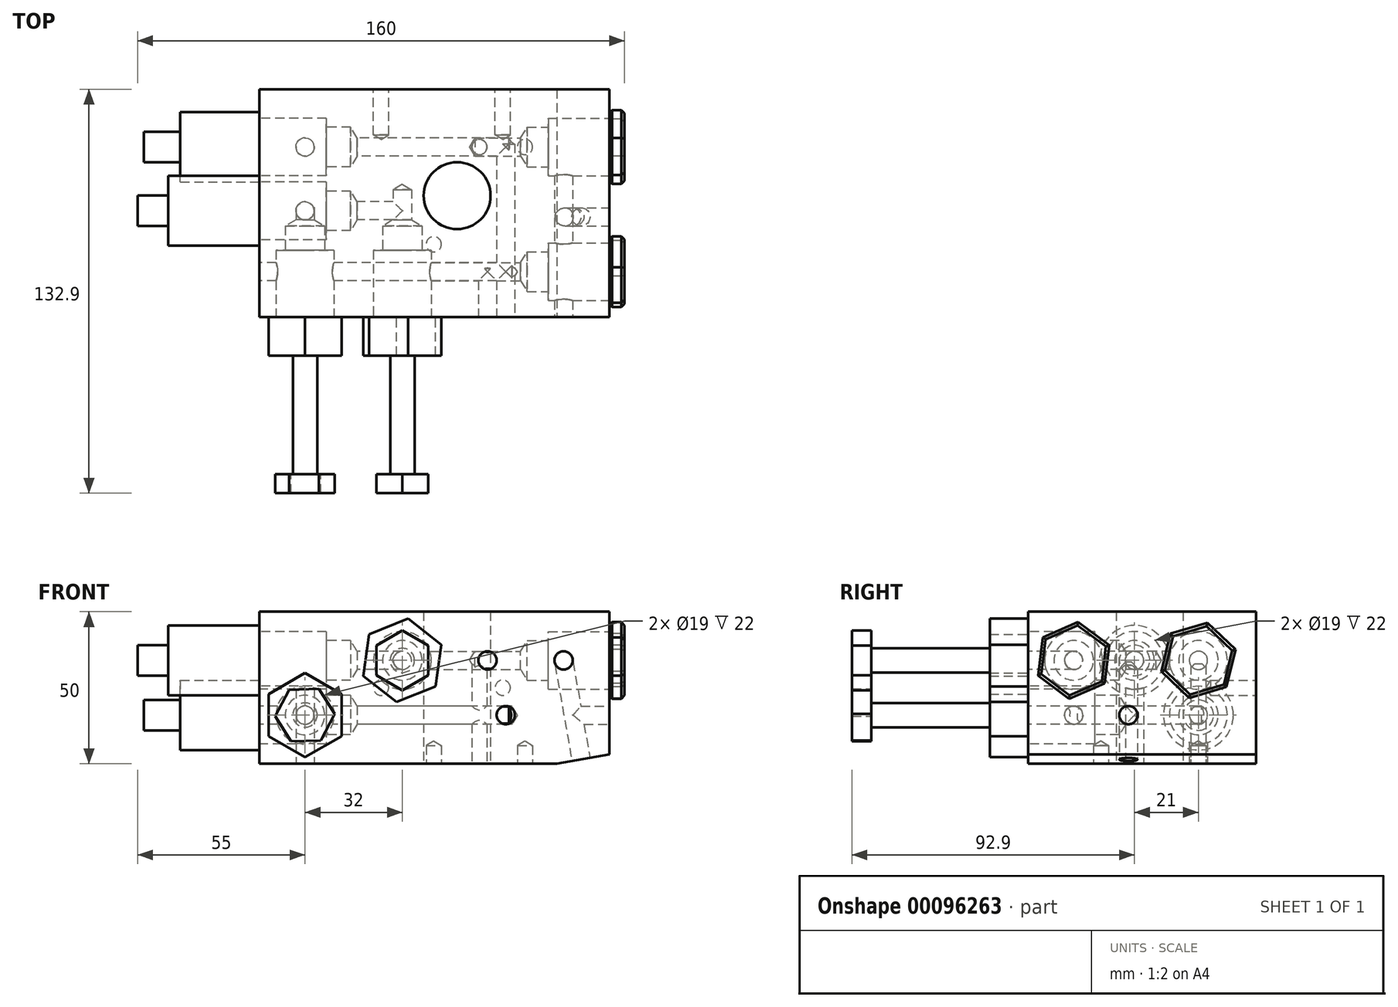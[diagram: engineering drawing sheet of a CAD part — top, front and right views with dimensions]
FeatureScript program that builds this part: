
annotation { "Feature Type Name" : "Feature", "Feature Type Description" : "" }
export const myFeature = defineFeature(function(context is Context, id is Id, definition is map)
    precondition{}
    {
        {
            var Q0;
            Q0=qCreatedBy(makeId("Top.planeOp"),FACE);
            var sketch = newSketch(context, id + "F0", { "sketchPlane" : qUnion([Q0])});
            skLineSegment(sketch, "E0.rect.bottom", {"start": v(50, 35) * mm, "end": v(-65, 35) * mm});
            skLineSegment(sketch, "E0.rect.top", {"start": v(50, -40) * mm, "end": v(-65, -40) * mm});
            skLineSegment(sketch, "E0.rect.left", {"start": v(50, 35) * mm, "end": v(50, -40) * mm});
            skLineSegment(sketch, "E0.rect.right", {"start": v(-65, 35) * mm, "end": v(-65, -40) * mm});
            skPoint(sketch, "E0.rect.middle", {"position": v(0, 0) * mm});
            skSolve(sketch);
        }
        {
            var Q0;
            Q0=makeQuery(id+"F0.imprint","IMPRINT",FACE,{"disambiguationData":[TD([[makeQuery(id+"F0.imprint","IMPRINT",EDGE,{"derivedFrom":sQuery(id+"F0.wireOp",EDGE,"E0.rect.bottom")}),1.0]])]});
            var Q1;
            Q1=makeQuery(id+"F0.imprint","IMPRINT",FACE,{"disambiguationData":[TD([[makeQuery(id+"F0.imprint","IMPRINT",EDGE,{"derivedFrom":sQuery(id+"F0.wireOp",EDGE,"7588558b-6d4b-4371-8287-17bf13519ebf.1.0.0")}),1.0]])]});
            var Q2;
            Q2=makeQuery(id+"F0.imprint","IMPRINT",FACE,{"disambiguationData":[TD([[makeQuery(id+"F0.imprint","IMPRINT",EDGE,{"derivedFrom":sQuery(id+"F0.wireOp",EDGE,"7588558b-6d4b-4371-8287-17bf13519ebf.1.1.0")}),1.0]])]});
            var Q3;
            Q3=makeQuery(id+"F0.imprint","IMPRINT",FACE,{"disambiguationData":[TD([[makeQuery(id+"F0.imprint","IMPRINT",EDGE,{"derivedFrom":sQuery(id+"F0.wireOp",EDGE,"f2f94a69-6f03-48d5-8e05-4ef8c2e551b9")}),1.0]])]});
            var Q4;
            Q4=makeQuery(id+"F0.imprint","IMPRINT",FACE,{"disambiguationData":[TD([[makeQuery(id+"F0.imprint","IMPRINT",EDGE,{"derivedFrom":sQuery(id+"F0.wireOp",EDGE,"7588558b-6d4b-4371-8287-17bf13519ebf.0.1.0")}),1.0]])]});
            extrude(context, id + "F1", {"entities" : qUnion([Q0, Q1, Q2, Q3, Q4]), "depth" : 50 * mm});
        }
        {
            var Q0;
            Q0=makeQuery(id+"F1.opExtrude","CAP_FACE",FACE,{"disambiguationData":[OSD([sQuery(id+"F0.wireOp",EDGE,"E0.rect.bottom"),sQuery(id+"F0.wireOp",EDGE,"E0.rect.top"),sQuery(id+"F0.wireOp",EDGE,"E0.rect.left"),sQuery(id+"F0.wireOp",EDGE,"E0.rect.right"),sQuery(id+"F0.wireOp",EDGE,"fc206ab4-4ad2-4e77-9b30-4fb9f0a5357b")])],"isStart":true});
            var sketch = newSketch(context, id + "F2", { "sketchPlane" : qUnion([Q0])});
            skCircle(sketch, "E1", {"center": v(22.32, -16) * mm, "radius": 2.75 * mm});
            skCircle(sketch, "E2", {"center": v(-7.68, 16) * mm, "radius": 2.75 * mm});
            skCircle(sketch, "E3", {"center": v(7.32, -16) * mm, "radius": 3 * mm});
            skPoint(sketch, "E4", {"position": v(-50, 5) * mm});
            skPoint(sketch, "E5", {"position": v(-50, -16) * mm});
            skLineSegment(sketch, "E6", {"start": v(7.32, -16) * mm, "end": v(44.16, -16) * mm, "construction": true});
            skLineSegment(sketch, "E7", {"start": v(7.32, -16) * mm, "end": v(7.32, 33.05) * mm, "construction": true});
            skPoint(sketch, "E8.0", {"position": v(0, 0) * mm});
            skLineSegment(sketch, "E9", {"start": v(-80.64, 0) * mm, "end": v(41.16, 0) * mm, "construction": true});
            skSolve(sketch);
        }
        {
            var Q0;
            Q0=sQuery(id+"F2.wireOp",VERTEX,"E3.center");
            var Q1;
            Q1=makeQuery(id+"F1.opExtrude","SWEPT_BODY",BODY,{"disambiguationData":[OSD([sQuery(id+"F0.wireOp",EDGE,"E0.rect.bottom"),sQuery(id+"F0.wireOp",EDGE,"E0.rect.top"),sQuery(id+"F0.wireOp",EDGE,"E0.rect.left"),sQuery(id+"F0.wireOp",EDGE,"E0.rect.right"),sQuery(id+"F0.wireOp",EDGE,"fc206ab4-4ad2-4e77-9b30-4fb9f0a5357b")])]});
            hole(context, id + "F3", {"style" : HoleStyle.SIMPLE, "holeDiameter" : 5 * mm, "endStyle" : HoleEndStyle.BLIND, "holeDepth" : 35 * mm, "locations" : qUnion([Q0]), "scope" : qUnion([Q1])});
        }
        {
            var Q0;
            Q0=makeQuery(id+"F1.opExtrude","SWEPT_FACE",FACE,{"disambiguationData":[OSD([sQuery(id+"F0.wireOp",EDGE,"E0.rect.left")])]});
            var sketch = newSketch(context, id + "F4", { "sketchPlane" : qUnion([Q0])});
            skLineSegment(sketch, "E10", {"start": v(-25, 34) * mm, "end": v(16, 34) * mm, "construction": true});
            skPoint(sketch, "E11", {"position": v(16, 34) * mm});
            skPoint(sketch, "E12", {"position": v(-25, 34) * mm});
            skCircle(sketch, "E13.cCircle", {"center": v(-25, 34) * mm, "radius": 11 * mm, "construction": true});
            skLineSegment(sketch, "E13.0", {"start": v(-35.19, 41.58) * mm, "end": v(-23.53, 46.62) * mm});
            skLineSegment(sketch, "E13.1", {"start": v(-23.53, 46.62) * mm, "end": v(-13.34, 39.03) * mm});
            skLineSegment(sketch, "E13.2", {"start": v(-13.34, 39.03) * mm, "end": v(-14.81, 26.42) * mm});
            skLineSegment(sketch, "E13.3", {"start": v(-14.81, 26.42) * mm, "end": v(-26.47, 21.38) * mm});
            skLineSegment(sketch, "E13.4", {"start": v(-26.47, 21.38) * mm, "end": v(-36.66, 28.97) * mm});
            skLineSegment(sketch, "E13.5", {"start": v(-36.66, 28.97) * mm, "end": v(-35.19, 41.58) * mm});
            skPoint(sketch, "E13.0.midPoint", {"position": v(-29.36, 44.1) * mm});
            skCircle(sketch, "E14.cCircle", {"center": v(16, 34) * mm, "radius": 11 * mm, "construction": true});
            skLineSegment(sketch, "E14.0", {"start": v(6.8, 42.75) * mm, "end": v(18.98, 46.35) * mm});
            skLineSegment(sketch, "E14.1", {"start": v(18.98, 46.35) * mm, "end": v(28.18, 37.6) * mm});
            skLineSegment(sketch, "E14.2", {"start": v(28.18, 37.6) * mm, "end": v(25.2, 25.25) * mm});
            skLineSegment(sketch, "E14.3", {"start": v(25.2, 25.25) * mm, "end": v(13.02, 21.65) * mm});
            skLineSegment(sketch, "E14.4", {"start": v(13.02, 21.65) * mm, "end": v(3.82, 30.4) * mm});
            skLineSegment(sketch, "E14.5", {"start": v(3.82, 30.4) * mm, "end": v(6.8, 42.75) * mm});
            skPoint(sketch, "E14.0.midPoint", {"position": v(12.89, 44.55) * mm});
            skPoint(sketch, "E15", {"position": v(-7, 16) * mm});
            skSolve(sketch);
        }
        {
            var Q0;
            Q0=sQuery(id+"F4.wireOp",VERTEX,"E11");
            var Q1;
            Q1=sQuery(id+"F4.wireOp",VERTEX,"E12");
            var Q2;
            Q2=makeQuery(id+"F1.opExtrude","SWEPT_BODY",BODY,{"disambiguationData":[OSD([sQuery(id+"F0.wireOp",EDGE,"E0.rect.bottom"),sQuery(id+"F0.wireOp",EDGE,"E0.rect.top"),sQuery(id+"F0.wireOp",EDGE,"E0.rect.left"),sQuery(id+"F0.wireOp",EDGE,"E0.rect.right"),sQuery(id+"F0.wireOp",EDGE,"fc206ab4-4ad2-4e77-9b30-4fb9f0a5357b")])]});
            hole(context, id + "F5", {"style" : HoleStyle.C_BORE, "endStyle" : HoleEndStyle.BLIND, "holeDiameter" : 13 * mm, "cBoreDiameter" : 19 * mm, "cBoreDepth" : 20 * mm, "holeDepth" : 27 * mm, "locations" : qUnion([Q0, Q1]), "scope" : qUnion([Q2])});
        }
        {
            var Q0;
            Q0=makeQuery(id+"F1.opExtrude","SWEPT_FACE",FACE,{"disambiguationData":[OSD([sQuery(id+"F0.wireOp",EDGE,"E0.rect.top")])]});
            var sketch = newSketch(context, id + "F6", { "sketchPlane" : qUnion([Q0])});
            skLineSegment(sketch, "E16", {"start": v(-65, 34) * mm, "end": v(50, 34) * mm, "construction": true});
            skLineSegment(sketch, "E17", {"start": v(-65, 16) * mm, "end": v(50, 16) * mm, "construction": true});
            skPoint(sketch, "E18", {"position": v(-50, 16) * mm});
            skPoint(sketch, "E19", {"position": v(-18, 34) * mm});
            skPoint(sketch, "E20", {"position": v(35, 34) * mm});
            skPoint(sketch, "E21", {"position": v(10, 34) * mm});
            skPoint(sketch, "E22", {"position": v(16, 16) * mm});
            skLineSegment(sketch, "E23", {"start": v(32.84, 0) * mm, "end": v(50, 3.03) * mm});
            skSolve(sketch);
        }
        {
            var Q0;
            Q0=sQuery(id+"F6.wireOp",VERTEX,"E22");
            var Q1;
            Q1=makeQuery(id+"F1.opExtrude","SWEPT_BODY",BODY,{"disambiguationData":[OSD([sQuery(id+"F0.wireOp",EDGE,"E0.rect.bottom"),sQuery(id+"F0.wireOp",EDGE,"E0.rect.top"),sQuery(id+"F0.wireOp",EDGE,"E0.rect.left"),sQuery(id+"F0.wireOp",EDGE,"E0.rect.right"),sQuery(id+"F0.wireOp",EDGE,"fc206ab4-4ad2-4e77-9b30-4fb9f0a5357b")])]});
            hole(context, id + "F7", {"style" : HoleStyle.SIMPLE, "holeDiameter" : 6 * mm, "endStyle" : HoleEndStyle.BLIND, "holeDepth" : 57 * mm, "locations" : qUnion([Q0]), "scope" : qUnion([Q1])});
        }
        {
            var Q0;
            Q0=makeQuery(id+"F1.opExtrude","SWEPT_FACE",FACE,{"disambiguationData":[OSD([sQuery(id+"F0.wireOp",EDGE,"E0.rect.right")])]});
            var sketch = newSketch(context, id + "F8", { "sketchPlane" : qUnion([Q0])});
            skPoint(sketch, "E24", {"position": v(25, 16) * mm});
            skPoint(sketch, "E25", {"position": v(5, 34) * mm});
            skPoint(sketch, "E26", {"position": v(-16, 16) * mm});
            skCircle(sketch, "E27", {"center": v(5, 34) * mm, "radius": 11.5 * mm});
            skSolve(sketch);
        }
        {
            var Q0;
            Q0=sQuery(id+"F8.wireOp",VERTEX,"E24");
            var Q1;
            Q1=makeQuery(id+"F1.opExtrude","SWEPT_BODY",BODY,{"disambiguationData":[OSD([sQuery(id+"F0.wireOp",EDGE,"E0.rect.bottom"),sQuery(id+"F0.wireOp",EDGE,"E0.rect.top"),sQuery(id+"F0.wireOp",EDGE,"E0.rect.left"),sQuery(id+"F0.wireOp",EDGE,"E0.rect.right"),sQuery(id+"F0.wireOp",EDGE,"fc206ab4-4ad2-4e77-9b30-4fb9f0a5357b")])]});
            hole(context, id + "F9", {"style" : HoleStyle.SIMPLE, "endStyle" : HoleEndStyle.BLIND, "holeDiameter" : 6 * mm, "holeDepth" : 83 * mm, "locations" : qUnion([Q0]), "scope" : qUnion([Q1])});
        }
        {
            var Q0;
            Q0=sQuery(id+"F6.wireOp",VERTEX,"E18");
            var Q1;
            Q1=sQuery(id+"F6.wireOp",VERTEX,"E19");
            var Q2;
            Q2=makeQuery(id+"F1.opExtrude","SWEPT_BODY",BODY,{"disambiguationData":[OSD([sQuery(id+"F0.wireOp",EDGE,"E0.rect.bottom"),sQuery(id+"F0.wireOp",EDGE,"E0.rect.top"),sQuery(id+"F0.wireOp",EDGE,"E0.rect.left"),sQuery(id+"F0.wireOp",EDGE,"E0.rect.right"),sQuery(id+"F0.wireOp",EDGE,"fc206ab4-4ad2-4e77-9b30-4fb9f0a5357b")])]});
            hole(context, id + "F10", {"style" : HoleStyle.C_BORE, "endStyle" : HoleEndStyle.BLIND, "holeDiameter" : 13 * mm, "cBoreDiameter" : 19 * mm, "cBoreDepth" : 22 * mm, "holeDepth" : 30 * mm, "locations" : qUnion([Q0, Q1]), "scope" : qUnion([Q2])});
        }
        {
            var Q0;
            Q0=sQuery(id+"F6.wireOp",VERTEX,"E18");
            var Q1;
            Q1=makeQuery(id+"F1.opExtrude","SWEPT_BODY",BODY,{"disambiguationData":[OSD([sQuery(id+"F0.wireOp",EDGE,"E0.rect.bottom"),sQuery(id+"F0.wireOp",EDGE,"E0.rect.top"),sQuery(id+"F0.wireOp",EDGE,"E0.rect.left"),sQuery(id+"F0.wireOp",EDGE,"E0.rect.right"),sQuery(id+"F0.wireOp",EDGE,"fc206ab4-4ad2-4e77-9b30-4fb9f0a5357b")])]});
            hole(context, id + "F11", {"style" : HoleStyle.SIMPLE, "endStyle" : HoleEndStyle.BLIND, "holeDiameter" : 6 * mm, "holeDepth" : 4 * mm, "locations" : qUnion([Q0]), "scope" : qUnion([Q1])});
        }
        {
            var Q0;
            Q0=sQuery(id+"F4.wireOp",VERTEX,"E11");
            var Q1;
            Q1=makeQuery(id+"F1.opExtrude","SWEPT_BODY",BODY,{"disambiguationData":[OSD([sQuery(id+"F0.wireOp",EDGE,"E0.rect.bottom"),sQuery(id+"F0.wireOp",EDGE,"E0.rect.top"),sQuery(id+"F0.wireOp",EDGE,"E0.rect.left"),sQuery(id+"F0.wireOp",EDGE,"E0.rect.right"),sQuery(id+"F0.wireOp",EDGE,"fc206ab4-4ad2-4e77-9b30-4fb9f0a5357b")])]});
            hole(context, id + "F12", {"style" : HoleStyle.SIMPLE, "endStyle" : HoleEndStyle.BLIND, "holeDiameter" : 6 * mm, "holeDepth" : 15 * mm, "locations" : qUnion([Q0]), "scope" : qUnion([Q1])});
        }
        {
            var Q0;
            Q0=sQuery(id+"F6.wireOp",VERTEX,"E21");
            var Q1;
            Q1=makeQuery(id+"F1.opExtrude","SWEPT_BODY",BODY,{"disambiguationData":[OSD([sQuery(id+"F0.wireOp",EDGE,"E0.rect.bottom"),sQuery(id+"F0.wireOp",EDGE,"E0.rect.top"),sQuery(id+"F0.wireOp",EDGE,"E0.rect.left"),sQuery(id+"F0.wireOp",EDGE,"E0.rect.right"),sQuery(id+"F0.wireOp",EDGE,"fc206ab4-4ad2-4e77-9b30-4fb9f0a5357b")])]});
            hole(context, id + "F13", {"style" : HoleStyle.SIMPLE, "endStyle" : HoleEndStyle.BLIND, "holeDiameter" : 6 * mm, "holeDepth" : 16 * mm, "locations" : qUnion([Q0]), "scope" : qUnion([Q1])});
        }
        {
            var Q0;
            Q0=sQuery(id+"F4.wireOp",VERTEX,"E12");
            var Q1;
            Q1=makeQuery(id+"F1.opExtrude","SWEPT_BODY",BODY,{"disambiguationData":[OSD([sQuery(id+"F0.wireOp",EDGE,"E0.rect.bottom"),sQuery(id+"F0.wireOp",EDGE,"E0.rect.top"),sQuery(id+"F0.wireOp",EDGE,"E0.rect.left"),sQuery(id+"F0.wireOp",EDGE,"E0.rect.right"),sQuery(id+"F0.wireOp",EDGE,"fc206ab4-4ad2-4e77-9b30-4fb9f0a5357b")])]});
            hole(context, id + "F14", {"style" : HoleStyle.SIMPLE, "endStyle" : HoleEndStyle.BLIND, "holeDiameter" : 6 * mm, "holeDepth" : 30 * mm, "locations" : qUnion([Q0]), "scope" : qUnion([Q1])});
        }
        {
            var Q0;
            Q0=sQuery(id+"F6.wireOp",VERTEX,"E20");
            var Q1;
            Q1=makeQuery(id+"F1.opExtrude","SWEPT_BODY",BODY,{"disambiguationData":[OSD([sQuery(id+"F0.wireOp",EDGE,"E0.rect.bottom"),sQuery(id+"F0.wireOp",EDGE,"E0.rect.top"),sQuery(id+"F0.wireOp",EDGE,"E0.rect.left"),sQuery(id+"F0.wireOp",EDGE,"E0.rect.right"),sQuery(id+"F0.wireOp",EDGE,"fc206ab4-4ad2-4e77-9b30-4fb9f0a5357b")])]});
            hole(context, id + "F15", {"style" : HoleStyle.SIMPLE, "endStyle" : HoleEndStyle.BLIND, "holeDiameter" : 6 * mm, "holeDepth" : 50 * mm, "locations" : qUnion([Q0]), "scope" : qUnion([Q1])});
        }
        {
            var Q0;
            Q0=sQuery(id+"F8.wireOp",VERTEX,"E25");
            var Q1;
            Q1=makeQuery(id+"F1.opExtrude","SWEPT_BODY",BODY,{"disambiguationData":[OSD([sQuery(id+"F0.wireOp",EDGE,"E0.rect.bottom"),sQuery(id+"F0.wireOp",EDGE,"E0.rect.top"),sQuery(id+"F0.wireOp",EDGE,"E0.rect.left"),sQuery(id+"F0.wireOp",EDGE,"E0.rect.right"),sQuery(id+"F0.wireOp",EDGE,"fc206ab4-4ad2-4e77-9b30-4fb9f0a5357b")])]});
            hole(context, id + "F16", {"style" : HoleStyle.C_BORE, "endStyle" : HoleEndStyle.BLIND, "holeDiameter" : 13 * mm, "cBoreDiameter" : 19 * mm, "cBoreDepth" : 22 * mm, "holeDepth" : 30 * mm, "locations" : qUnion([Q0]), "scope" : qUnion([Q1])});
        }
        {
            var Q0;
            Q0=sQuery(id+"F8.wireOp",VERTEX,"E26");
            var Q1;
            Q1=makeQuery(id+"F1.opExtrude","SWEPT_BODY",BODY,{"disambiguationData":[OSD([sQuery(id+"F0.wireOp",EDGE,"E0.rect.bottom"),sQuery(id+"F0.wireOp",EDGE,"E0.rect.top"),sQuery(id+"F0.wireOp",EDGE,"E0.rect.left"),sQuery(id+"F0.wireOp",EDGE,"E0.rect.right")])]});
            hole(context, id + "F17", {"style" : HoleStyle.C_BORE, "endStyle" : HoleEndStyle.BLIND, "holeDiameter" : 13 * mm, "cBoreDiameter" : 19 * mm, "cBoreDepth" : 22 * mm, "holeDepth" : 30 * mm, "startFromSketch" : true, "locations" : qUnion([Q0]), "scope" : qUnion([Q1])});
        }
        {
            var Q0;
            Q0=sQuery(id+"F8.wireOp",VERTEX,"E25");
            var Q1;
            Q1=makeQuery(id+"F1.opExtrude","SWEPT_BODY",BODY,{"disambiguationData":[OSD([sQuery(id+"F0.wireOp",EDGE,"E0.rect.bottom"),sQuery(id+"F0.wireOp",EDGE,"E0.rect.top"),sQuery(id+"F0.wireOp",EDGE,"E0.rect.left"),sQuery(id+"F0.wireOp",EDGE,"E0.rect.right"),sQuery(id+"F0.wireOp",EDGE,"fc206ab4-4ad2-4e77-9b30-4fb9f0a5357b")])]});
            hole(context, id + "F18", {"style" : HoleStyle.SIMPLE, "endStyle" : HoleEndStyle.BLIND, "holeDiameter" : 6 * mm, "holeDepth" : 15 * mm, "locations" : qUnion([Q0]), "scope" : qUnion([Q1])});
        }
        {
            var Q0;
            Q0=sQuery(id+"F2.wireOp",VERTEX,"E4");
            var Q1;
            Q1=makeQuery(id+"F1.opExtrude","SWEPT_BODY",BODY,{"disambiguationData":[OSD([sQuery(id+"F0.wireOp",EDGE,"E0.rect.bottom"),sQuery(id+"F0.wireOp",EDGE,"E0.rect.top"),sQuery(id+"F0.wireOp",EDGE,"E0.rect.left"),sQuery(id+"F0.wireOp",EDGE,"E0.rect.right"),sQuery(id+"F0.wireOp",EDGE,"fc206ab4-4ad2-4e77-9b30-4fb9f0a5357b")])]});
            hole(context, id + "F19", {"style" : HoleStyle.SIMPLE, "endStyle" : HoleEndStyle.BLIND, "holeDiameter" : 6 * mm, "holeDepth" : 35 * mm, "locations" : qUnion([Q0]), "scope" : qUnion([Q1])});
        }
        {
            var Q0;
            Q0=sQuery(id+"F6.wireOp",VERTEX,"E19");
            var Q1;
            Q1=makeQuery(id+"F1.opExtrude","SWEPT_BODY",BODY,{"disambiguationData":[OSD([sQuery(id+"F0.wireOp",EDGE,"E0.rect.bottom"),sQuery(id+"F0.wireOp",EDGE,"E0.rect.top"),sQuery(id+"F0.wireOp",EDGE,"E0.rect.left"),sQuery(id+"F0.wireOp",EDGE,"E0.rect.right"),sQuery(id+"F0.wireOp",EDGE,"fc206ab4-4ad2-4e77-9b30-4fb9f0a5357b")])]});
            hole(context, id + "F20", {"style" : HoleStyle.SIMPLE, "endStyle" : HoleEndStyle.BLIND, "holeDiameter" : 6 * mm, "holeDepth" : 4 * mm, "locations" : qUnion([Q0]), "scope" : qUnion([Q1])});
        }
        {
            var Q0;
            Q0=makeQuery(id+"F1.opExtrude","SWEPT_FACE",FACE,{"disambiguationData":[OSD([sQuery(id+"F0.wireOp",EDGE,"E0.rect.bottom")])]});
            var sketch = newSketch(context, id + "F21", { "sketchPlane" : qUnion([Q0])});
            skPoint(sketch, "E28", {"position": v(-15, 25) * mm});
            skPoint(sketch, "E29.1.0.0", {"position": v(25, 25) * mm});
            skLineSegment(sketch, "E29.direction1", {"start": v(-15, 25) * mm, "end": v(25, 25) * mm, "construction": true});
            skSolve(sketch);
        }
        {
            var Q0;
            Q0=sQuery(id+"F21.wireOp",VERTEX,"E29.1.0.0");
            var Q1;
            Q1=sQuery(id+"F21.wireOp",VERTEX,"E28");
            var Q2;
            Q2=makeQuery(id+"F1.opExtrude","SWEPT_BODY",BODY,{"disambiguationData":[OSD([sQuery(id+"F0.wireOp",EDGE,"E0.rect.bottom"),sQuery(id+"F0.wireOp",EDGE,"E0.rect.top"),sQuery(id+"F0.wireOp",EDGE,"E0.rect.left"),sQuery(id+"F0.wireOp",EDGE,"E0.rect.right"),sQuery(id+"F0.wireOp",EDGE,"fc206ab4-4ad2-4e77-9b30-4fb9f0a5357b")])]});
            hole(context, id + "F22", {"style" : HoleStyle.SIMPLE, "endStyle" : HoleEndStyle.BLIND, "holeDiameter" : 5 * mm, "holeDepth" : 15 * mm, "locations" : qUnion([Q0, Q1]), "scope" : qUnion([Q2])});
        }
        {
            var Q0;
            Q0=sQuery(id+"F0.wireOp",VERTEX,"E0.rect.middle");
            var Q1;
            Q1=makeQuery(id+"F1.opExtrude","SWEPT_BODY",BODY,{"disambiguationData":[OSD([sQuery(id+"F0.wireOp",EDGE,"E0.rect.bottom"),sQuery(id+"F0.wireOp",EDGE,"E0.rect.top"),sQuery(id+"F0.wireOp",EDGE,"E0.rect.left"),sQuery(id+"F0.wireOp",EDGE,"E0.rect.right")])]});
            hole(context, id + "F23", {"style" : HoleStyle.SIMPLE, "endStyle" : HoleEndStyle.THROUGH, "oppositeDirection" : true, "holeDiameter" : 22 * mm, "locations" : qUnion([Q0]), "scope" : qUnion([Q1]), "isTappedThrough" : true});
        }
        {
            var Q0;
            {var subQ0=sQuery(id+"F0.wireOp",EDGE,"E0.rect.right");Q0=makeQuery(id+"F8.imprint","IMPRINT",FACE,{"disambiguationData":[TD([[makeQuery(id+"F8.imprint","IMPRINT",EDGE,{"derivedFrom":makeQuery(id+"F1.opExtrude","CAP_EDGE",EDGE,{"disambiguationData":[OSD([subQ0])],"isStart":true})}),1.0]])]});}
            var sketch = newSketch(context, id + "F24", { "sketchPlane" : qUnion([Q0])});
            skCircle(sketch, "E30", {"center": v(-16, 16) * mm, "radius": 11.5 * mm});
            skSolve(sketch);
        }
        {
            var Q0;
            Q0=makeQuery(id+"F24.imprint","IMPRINT",FACE,{"disambiguationData":[TD([[makeQuery(id+"F24.imprint","IMPRINT",EDGE,{"derivedFrom":sQuery(id+"F24.wireOp",EDGE,"E30")}),1.0]])]});
            extrude(context, id + "F25", {"entities" : qUnion([Q0]), "depth" : 26 * mm});
        }
        {
            var Q0;
            Q0=makeQuery(id+"F25.opExtrude","CAP_FACE",FACE,{"disambiguationData":[OSD([sQuery(id+"F24.wireOp",EDGE,"E30")])],"isStart":false});
            var sketch = newSketch(context, id + "F26", { "sketchPlane" : qUnion([Q0])});
            skCircle(sketch, "E31", {"center": v(-16, 16) * mm, "radius": 5 * mm});
            skSolve(sketch);
        }
        {
            var Q0;
            Q0=sQuery(id+"F8.wireOp",VERTEX,"E26");
            var Q1;
            Q1=makeQuery(id+"F1.opExtrude","SWEPT_BODY",BODY,{"disambiguationData":[OSD([sQuery(id+"F0.wireOp",EDGE,"E0.rect.bottom"),sQuery(id+"F0.wireOp",EDGE,"E0.rect.top"),sQuery(id+"F0.wireOp",EDGE,"E0.rect.left"),sQuery(id+"F0.wireOp",EDGE,"E0.rect.right")])]});
            hole(context, id + "F27", {"style" : HoleStyle.SIMPLE, "endStyle" : HoleEndStyle.BLIND, "holeDiameter" : 6 * mm, "holeDepth" : 82 * mm, "startFromSketch" : true, "locations" : qUnion([Q0]), "scope" : qUnion([Q1])});
        }
        {
            var Q0;
            Q0=makeQuery(id+"F4.imprint","IMPRINT",FACE,{"disambiguationData":[TD([[makeQuery(id+"F4.imprint","IMPRINT",EDGE,{"derivedFrom":sQuery(id+"F4.wireOp",EDGE,"E13.0")}),-1.0]])]});
            var Q1;
            Q1=makeQuery(id+"F4.imprint","IMPRINT",FACE,{"disambiguationData":[TD([[makeQuery(id+"F4.imprint","IMPRINT",EDGE,{"derivedFrom":sQuery(id+"F4.wireOp",EDGE,"E14.0")}),-1.0]])]});
            extrude(context, id + "F28", {"entities" : qUnion([Q0, Q1]), "depth" : 5 * mm});
        }
        {
            var Q0;
            Q0=makeQuery(id+"F28.opExtrude","CAP_EDGE",EDGE,{"disambiguationData":[OSD([sQuery(id+"F4.wireOp",EDGE,"E13.3")])],"isStart":true});
            var Q1;
            Q1=makeQuery(id+"F28.opExtrude","CAP_EDGE",EDGE,{"disambiguationData":[OSD([sQuery(id+"F4.wireOp",EDGE,"E13.4")])],"isStart":true});
            var Q2;
            Q2=makeQuery(id+"F28.opExtrude","CAP_EDGE",EDGE,{"disambiguationData":[OSD([sQuery(id+"F4.wireOp",EDGE,"E13.5")])],"isStart":true});
            var Q3;
            Q3=makeQuery(id+"F28.opExtrude","CAP_EDGE",EDGE,{"disambiguationData":[OSD([sQuery(id+"F4.wireOp",EDGE,"E13.4")])],"isStart":false});
            var Q4;
            Q4=makeQuery(id+"F28.opExtrude","CAP_EDGE",EDGE,{"disambiguationData":[OSD([sQuery(id+"F4.wireOp",EDGE,"E13.3")])],"isStart":false});
            var Q5;
            Q5=makeQuery(id+"F28.opExtrude","CAP_EDGE",EDGE,{"disambiguationData":[OSD([sQuery(id+"F4.wireOp",EDGE,"E13.2")])],"isStart":false});
            var Q6;
            Q6=makeQuery(id+"F28.opExtrude","CAP_EDGE",EDGE,{"disambiguationData":[OSD([sQuery(id+"F4.wireOp",EDGE,"E13.1")])],"isStart":false});
            var Q7;
            Q7=makeQuery(id+"F28.opExtrude","CAP_EDGE",EDGE,{"disambiguationData":[OSD([sQuery(id+"F4.wireOp",EDGE,"E13.0")])],"isStart":false});
            var Q8;
            Q8=makeQuery(id+"F28.opExtrude","CAP_EDGE",EDGE,{"disambiguationData":[OSD([sQuery(id+"F4.wireOp",EDGE,"E13.5")])],"isStart":false});
            var Q9;
            Q9=makeQuery(id+"F28.opExtrude","CAP_EDGE",EDGE,{"disambiguationData":[OSD([sQuery(id+"F4.wireOp",EDGE,"E13.0")])],"isStart":true});
            var Q10;
            Q10=makeQuery(id+"F28.opExtrude","CAP_EDGE",EDGE,{"disambiguationData":[OSD([sQuery(id+"F4.wireOp",EDGE,"E13.1")])],"isStart":true});
            var Q11;
            Q11=makeQuery(id+"F28.opExtrude","CAP_EDGE",EDGE,{"disambiguationData":[OSD([sQuery(id+"F4.wireOp",EDGE,"E13.2")])],"isStart":true});
            var Q12;
            Q12=makeQuery(id+"F28.opExtrude","CAP_EDGE",EDGE,{"disambiguationData":[OSD([sQuery(id+"F4.wireOp",EDGE,"E14.4")])],"isStart":false});
            var Q13;
            Q13=makeQuery(id+"F28.opExtrude","CAP_EDGE",EDGE,{"disambiguationData":[OSD([sQuery(id+"F4.wireOp",EDGE,"E14.4")])],"isStart":true});
            var Q14;
            Q14=makeQuery(id+"F28.opExtrude","CAP_EDGE",EDGE,{"disambiguationData":[OSD([sQuery(id+"F4.wireOp",EDGE,"E14.3")])],"isStart":false});
            var Q15;
            Q15=makeQuery(id+"F28.opExtrude","CAP_EDGE",EDGE,{"disambiguationData":[OSD([sQuery(id+"F4.wireOp",EDGE,"E14.3")])],"isStart":true});
            var Q16;
            Q16=makeQuery(id+"F28.opExtrude","CAP_EDGE",EDGE,{"disambiguationData":[OSD([sQuery(id+"F4.wireOp",EDGE,"E14.2")])],"isStart":false});
            var Q17;
            Q17=makeQuery(id+"F28.opExtrude","CAP_EDGE",EDGE,{"disambiguationData":[OSD([sQuery(id+"F4.wireOp",EDGE,"E14.2")])],"isStart":true});
            var Q18;
            Q18=makeQuery(id+"F28.opExtrude","CAP_EDGE",EDGE,{"disambiguationData":[OSD([sQuery(id+"F4.wireOp",EDGE,"E14.1")])],"isStart":false});
            var Q19;
            Q19=makeQuery(id+"F28.opExtrude","CAP_EDGE",EDGE,{"disambiguationData":[OSD([sQuery(id+"F4.wireOp",EDGE,"E14.1")])],"isStart":true});
            var Q20;
            Q20=makeQuery(id+"F28.opExtrude","CAP_EDGE",EDGE,{"disambiguationData":[OSD([sQuery(id+"F4.wireOp",EDGE,"E14.5")])],"isStart":false});
            var Q21;
            Q21=makeQuery(id+"F28.opExtrude","CAP_EDGE",EDGE,{"disambiguationData":[OSD([sQuery(id+"F4.wireOp",EDGE,"E14.5")])],"isStart":true});
            var Q22;
            Q22=makeQuery(id+"F28.opExtrude","CAP_EDGE",EDGE,{"disambiguationData":[OSD([sQuery(id+"F4.wireOp",EDGE,"E14.0")])],"isStart":true});
            var Q23;
            Q23=makeQuery(id+"F28.opExtrude","CAP_EDGE",EDGE,{"disambiguationData":[OSD([sQuery(id+"F4.wireOp",EDGE,"E14.0")])],"isStart":false});
            chamfer(context, id + "F29", {"entities" : qUnion([Q0, Q1, Q2, Q3, Q4, Q5, Q6, Q7, Q8, Q9, Q10, Q11, Q12, Q13, Q14, Q15, Q16, Q17, Q18, Q19, Q20, Q21, Q22, Q23]), "width" : 1 * mm, "tangentPropagation" : true});
        }
        {
            var Q0;
            Q0=makeQuery(id+"F26.imprint","IMPRINT",FACE,{"disambiguationData":[TD([[makeQuery(id+"F26.imprint","IMPRINT",EDGE,{"derivedFrom":sQuery(id+"F26.wireOp",EDGE,"E31")}),1.0]])]});
            extrude(context, id + "F30", {"entities" : qUnion([Q0]), "operationType" : NewBodyOperationType.ADD, "depth" : 12 * mm});
        }
        {
            var Q0;
            Q0=makeQuery(id+"F8.imprint","IMPRINT",FACE,{"disambiguationData":[TD([[makeQuery(id+"F8.imprint","IMPRINT",EDGE,{"derivedFrom":sQuery(id+"F8.wireOp",EDGE,"E27")}),1.0]])]});
            extrude(context, id + "F31", {"entities" : qUnion([Q0]), "depth" : 30 * mm});
        }
        {
            var Q0;
            Q0=makeQuery(id+"F31.opExtrude","CAP_FACE",FACE,{"disambiguationData":[OSD([sQuery(id+"F8.wireOp",EDGE,"E27")])],"isStart":false});
            var sketch = newSketch(context, id + "F32", { "sketchPlane" : qUnion([Q0])});
            skCircle(sketch, "E32", {"center": v(5, 34) * mm, "radius": 5 * mm});
            skSolve(sketch);
        }
        {
            var Q0;
            Q0=makeQuery(id+"F32.imprint","IMPRINT",FACE,{"disambiguationData":[TD([[makeQuery(id+"F32.imprint","IMPRINT",EDGE,{"derivedFrom":sQuery(id+"F32.wireOp",EDGE,"E32")}),1.0]])]});
            extrude(context, id + "F33", {"entities" : qUnion([Q0]), "operationType" : NewBodyOperationType.ADD, "depth" : 10 * mm});
        }
        {
            var Q0;
            Q0=sQuery(id+"F2.wireOp",VERTEX,"E5");
            var Q1;
            Q1=makeQuery(id+"F1.opExtrude","SWEPT_BODY",BODY,{"disambiguationData":[OSD([sQuery(id+"F0.wireOp",EDGE,"E0.rect.bottom"),sQuery(id+"F0.wireOp",EDGE,"E0.rect.top"),sQuery(id+"F0.wireOp",EDGE,"E0.rect.left"),sQuery(id+"F0.wireOp",EDGE,"E0.rect.right")])]});
            hole(context, id + "F34", {"style" : HoleStyle.SIMPLE, "endStyle" : HoleEndStyle.BLIND, "holeDiameter" : 6 * mm, "holeDepth" : 18 * mm, "locations" : qUnion([Q0]), "scope" : qUnion([Q1])});
        }
        {
            var Q0;
            {var subQ0=sQuery(id+"F0.wireOp",EDGE,"E0.rect.top");Q0=makeQuery(id+"F6.imprint","IMPRINT",FACE,{"disambiguationData":[TD([[makeQuery(id+"F6.imprint","IMPRINT",EDGE,{"derivedFrom":makeQuery(id+"F1.opExtrude","CAP_EDGE",EDGE,{"disambiguationData":[OSD([subQ0])],"isStart":true})}),-1.0]])]});}
            var sketch = newSketch(context, id + "F35", { "sketchPlane" : qUnion([Q0])});
            skCircle(sketch, "E33.cCircle", {"center": v(-50, 16) * mm, "radius": 12 * mm, "construction": true});
            skLineSegment(sketch, "E33.0", {"start": v(-38, 22.93) * mm, "end": v(-38, 9.07) * mm});
            skLineSegment(sketch, "E33.1", {"start": v(-38, 9.07) * mm, "end": v(-50, 2.14) * mm});
            skLineSegment(sketch, "E33.2", {"start": v(-50, 2.14) * mm, "end": v(-62, 9.07) * mm});
            skLineSegment(sketch, "E33.3", {"start": v(-62, 9.07) * mm, "end": v(-62, 22.93) * mm});
            skLineSegment(sketch, "E33.4", {"start": v(-62, 22.93) * mm, "end": v(-50, 29.86) * mm});
            skLineSegment(sketch, "E33.5", {"start": v(-50, 29.86) * mm, "end": v(-38, 22.93) * mm});
            skPoint(sketch, "E33.0.midPoint", {"position": v(-38, 16) * mm});
            skCircle(sketch, "E34.cCircle", {"center": v(-18, 34) * mm, "radius": 12 * mm, "construction": true});
            skLineSegment(sketch, "E34.0", {"start": v(-5.15, 39.18) * mm, "end": v(-7.1, 25.46) * mm});
            skLineSegment(sketch, "E34.1", {"start": v(-7.1, 25.46) * mm, "end": v(-19.94, 20.28) * mm});
            skLineSegment(sketch, "E34.2", {"start": v(-19.94, 20.28) * mm, "end": v(-30.85, 28.82) * mm});
            skLineSegment(sketch, "E34.3", {"start": v(-30.85, 28.82) * mm, "end": v(-28.9, 42.54) * mm});
            skLineSegment(sketch, "E34.4", {"start": v(-28.9, 42.54) * mm, "end": v(-16.06, 47.72) * mm});
            skLineSegment(sketch, "E34.5", {"start": v(-16.06, 47.72) * mm, "end": v(-5.15, 39.18) * mm});
            skPoint(sketch, "E34.0.midPoint", {"position": v(-6.12, 32.32) * mm});
            skSolve(sketch);
        }
        {
            var Q0;
            Q0=qSketchRegion(id+"F35",true);
            extrude(context, id + "F36", {"entities" : qUnion([Q0]), "depth" : 12.6 * mm});
        }
        {
            var Q0;
            Q0=makeQuery(id+"F36.opExtrude","CAP_FACE",FACE,{"disambiguationData":[OSD([sQuery(id+"F35.wireOp",EDGE,"E33.0"),sQuery(id+"F35.wireOp",EDGE,"E33.1"),sQuery(id+"F35.wireOp",EDGE,"E33.2"),sQuery(id+"F35.wireOp",EDGE,"E33.3"),sQuery(id+"F35.wireOp",EDGE,"E33.4"),sQuery(id+"F35.wireOp",EDGE,"E33.5")])],"isStart":false});
            var sketch = newSketch(context, id + "F37", { "sketchPlane" : qUnion([Q0])});
            skCircle(sketch, "E35", {"center": v(-50, 16) * mm, "radius": 4 * mm});
            skPoint(sketch, "E35.centerSnap0", {"position": v(-62, 16) * mm});
            skSolve(sketch);
        }
        {
            var Q0;
            Q0=makeQuery(id+"F37.imprint","IMPRINT",FACE,{"disambiguationData":[TD([[makeQuery(id+"F37.imprint","IMPRINT",EDGE,{"derivedFrom":sQuery(id+"F37.wireOp",EDGE,"E35")}),1.0]])]});
            extrude(context, id + "F38", {"entities" : qUnion([Q0]), "operationType" : NewBodyOperationType.ADD, "depth" : 39 * mm});
        }
        {
            var Q0;
            Q0=makeQuery(id+"F38.opExtrude","CAP_FACE",FACE,{"disambiguationData":[OSD([sQuery(id+"F37.wireOp",EDGE,"E35")])],"isStart":false});
            var sketch = newSketch(context, id + "F39", { "sketchPlane" : qUnion([Q0])});
            skCircle(sketch, "E36.cCircle", {"center": v(-50, 16) * mm, "radius": 8.5 * mm, "construction": true});
            skLineSegment(sketch, "E36.0", {"start": v(-45.41, 24.68) * mm, "end": v(-40.2, 16.37) * mm});
            skLineSegment(sketch, "E36.1", {"start": v(-40.2, 16.37) * mm, "end": v(-44.78, 7.69) * mm});
            skLineSegment(sketch, "E36.2", {"start": v(-44.78, 7.69) * mm, "end": v(-54.59, 7.32) * mm});
            skLineSegment(sketch, "E36.3", {"start": v(-54.59, 7.32) * mm, "end": v(-59.8, 15.63) * mm});
            skLineSegment(sketch, "E36.4", {"start": v(-59.8, 15.63) * mm, "end": v(-55.22, 24.31) * mm});
            skLineSegment(sketch, "E36.5", {"start": v(-55.22, 24.31) * mm, "end": v(-45.41, 24.68) * mm});
            skPoint(sketch, "E36.0.midPoint", {"position": v(-42.8, 20.52) * mm});
            skSolve(sketch);
        }
        {
            var Q0;
            Q0=makeQuery(id+"F39.imprint","IMPRINT",FACE,{"disambiguationData":[TD([[makeQuery(id+"F39.imprint","IMPRINT",EDGE,{"derivedFrom":sQuery(id+"F39.wireOp",EDGE,"E36.0")}),-1.0]])]});
            var Q1;
            Q1=makeQuery(id+"F39.imprint","IMPRINT",FACE,{"disambiguationData":[TD([[makeQuery(id+"F39.imprint","IMPRINT",EDGE,{"derivedFrom":makeQuery(id+"F38.opExtrude","CAP_EDGE",EDGE,{"disambiguationData":[OSD([sQuery(id+"F37.wireOp",EDGE,"E35")])],"isStart":false})}),1.0]])]});
            extrude(context, id + "F40", {"entities" : qUnion([Q0, Q1]), "operationType" : NewBodyOperationType.ADD, "depth" : 6.3 * mm});
        }
        {
            var Q0;
            Q0=makeQuery(id+"F36.opExtrude","CAP_FACE",FACE,{"disambiguationData":[OSD([sQuery(id+"F35.wireOp",EDGE,"E34.0"),sQuery(id+"F35.wireOp",EDGE,"E34.1"),sQuery(id+"F35.wireOp",EDGE,"E34.2"),sQuery(id+"F35.wireOp",EDGE,"E34.3"),sQuery(id+"F35.wireOp",EDGE,"E34.4"),sQuery(id+"F35.wireOp",EDGE,"E34.5")])],"isStart":false});
            var sketch = newSketch(context, id + "F41", { "sketchPlane" : qUnion([Q0])});
            skLineSegment(sketch, "E37", {"start": v(-13.52, 22.87) * mm, "end": v(-22.48, 45.13) * mm, "construction": true});
            skCircle(sketch, "E38", {"center": v(-18, 34) * mm, "radius": 4 * mm});
            skSolve(sketch);
        }
        {
            var Q0;
            Q0=makeQuery(id+"F41.imprint","IMPRINT",FACE,{"disambiguationData":[TD([[makeQuery(id+"F41.imprint","IMPRINT",EDGE,{"derivedFrom":sQuery(id+"F41.wireOp",EDGE,"E38")}),1.0]])]});
            extrude(context, id + "F42", {"entities" : qUnion([Q0]), "operationType" : NewBodyOperationType.ADD, "depth" : 39 * mm});
        }
        {
            var Q0;
            Q0=makeQuery(id+"F42.opExtrude","CAP_FACE",FACE,{"disambiguationData":[OSD([sQuery(id+"F41.wireOp",EDGE,"E38")])],"isStart":false});
            var sketch = newSketch(context, id + "F43", { "sketchPlane" : qUnion([Q0])});
            skCircle(sketch, "E39.cCircle", {"center": v(-18, 34) * mm, "radius": 8.5 * mm, "construction": true});
            skLineSegment(sketch, "E39.0", {"start": v(-9.5, 38.9) * mm, "end": v(-9.5, 29.1) * mm});
            skLineSegment(sketch, "E39.1", {"start": v(-9.5, 29.1) * mm, "end": v(-18, 24.19) * mm});
            skLineSegment(sketch, "E39.2", {"start": v(-18, 24.19) * mm, "end": v(-26.5, 29.1) * mm});
            skLineSegment(sketch, "E39.3", {"start": v(-26.5, 29.1) * mm, "end": v(-26.5, 38.9) * mm});
            skLineSegment(sketch, "E39.4", {"start": v(-26.5, 38.9) * mm, "end": v(-18, 43.81) * mm});
            skLineSegment(sketch, "E39.5", {"start": v(-18, 43.81) * mm, "end": v(-9.5, 38.9) * mm});
            skPoint(sketch, "E39.0.midPoint", {"position": v(-9.5, 34) * mm});
            skSolve(sketch);
        }
        {
            var Q0;
            Q0=makeQuery(id+"F43.imprint","IMPRINT",FACE,{"disambiguationData":[TD([[makeQuery(id+"F43.imprint","IMPRINT",EDGE,{"derivedFrom":sQuery(id+"F43.wireOp",EDGE,"E39.0")}),-1.0]])]});
            var Q1;
            Q1=makeQuery(id+"F43.imprint","IMPRINT",FACE,{"disambiguationData":[TD([[makeQuery(id+"F43.imprint","IMPRINT",EDGE,{"derivedFrom":makeQuery(id+"F42.opExtrude","CAP_EDGE",EDGE,{"disambiguationData":[OSD([sQuery(id+"F41.wireOp",EDGE,"E38")])],"isStart":false})}),1.0]])]});
            extrude(context, id + "F44", {"entities" : qUnion([Q0, Q1]), "operationType" : NewBodyOperationType.ADD, "depth" : 6.3 * mm});
        }
        {
            var Q0;
            Q0=sQuery(id+"F2.wireOp",VERTEX,"E2.center");
            var Q1;
            Q1=sQuery(id+"F2.wireOp",VERTEX,"E1.center");
            var Q2;
            Q2=makeQuery(id+"F1.opExtrude","SWEPT_BODY",BODY,{"disambiguationData":[OSD([sQuery(id+"F0.wireOp",EDGE,"E0.rect.bottom"),sQuery(id+"F0.wireOp",EDGE,"E0.rect.top"),sQuery(id+"F0.wireOp",EDGE,"E0.rect.left"),sQuery(id+"F0.wireOp",EDGE,"E0.rect.right")])]});
            hole(context, id + "F45", {"style" : HoleStyle.SIMPLE, "endStyle" : HoleEndStyle.BLIND, "holeDiameter" : 5 * mm, "holeDepth" : 6 * mm, "locations" : qUnion([Q0, Q1]), "scope" : qUnion([Q2])});
        }
        {
            var Q0;
            {var subQ0=sQuery(id+"F6.wireOp",EDGE,"E23");Q0=makeQuery(id+"F6.imprint","IMPRINT",FACE,{"disambiguationData":[TD([[makeQuery(id+"F6.imprint","IMPRINT",EDGE,{"derivedFrom":subQ0}),-1.0]])]});}
            extrude(context, id + "F46", {"entities" : qUnion([Q0]), "operationType" : NewBodyOperationType.REMOVE, "endBound" : BoundingType.UP_TO_NEXT, "oppositeDirection" : true, "depth" : 25 * mm});
        }
        {
            var Q0;
            Q0=makeQuery(id+"F46.boolean.opBoolean","COPY",FACE,{"derivedFrom":makeQuery(id+"F46.opExtrude","SWEPT_FACE",FACE,{"disambiguationData":[OSD([sQuery(id+"F6.wireOp",EDGE,"E23")])]})});
            var sketch = newSketch(context, id + "F47", { "sketchPlane" : qUnion([Q0])});
            skPoint(sketch, "E40", {"position": v(40.34, 7) * mm});
            skSolve(sketch);
        }
        {
            var Q0;
            Q0=sQuery(id+"F47.wireOp",VERTEX,"E40");
            var Q1;
            Q1=makeQuery(id+"F1.opExtrude","SWEPT_BODY",BODY,{"disambiguationData":[OSD([sQuery(id+"F0.wireOp",EDGE,"E0.rect.bottom"),sQuery(id+"F0.wireOp",EDGE,"E0.rect.top"),sQuery(id+"F0.wireOp",EDGE,"E0.rect.left"),sQuery(id+"F0.wireOp",EDGE,"E0.rect.right")])]});
            hole(context, id + "F48", {"style" : HoleStyle.SIMPLE, "endStyle" : HoleEndStyle.BLIND, "holeDiameter" : 6 * mm, "holeDepth" : 32 * mm, "locations" : qUnion([Q0]), "scope" : qUnion([Q1])});
        }
        {
            var Q0;
            Q0=sQuery(id+"F4.wireOp",VERTEX,"E15");
            var Q1;
            Q1=makeQuery(id+"F1.opExtrude","SWEPT_BODY",BODY,{"disambiguationData":[OSD([sQuery(id+"F0.wireOp",EDGE,"E0.rect.bottom"),sQuery(id+"F0.wireOp",EDGE,"E0.rect.top"),sQuery(id+"F0.wireOp",EDGE,"E0.rect.left"),sQuery(id+"F0.wireOp",EDGE,"E0.rect.right")])]});
            hole(context, id + "F49", {"style" : HoleStyle.SIMPLE, "endStyle" : HoleEndStyle.BLIND, "holeDiameter" : 6 * mm, "holeDepth" : 12 * mm, "locations" : qUnion([Q0]), "scope" : qUnion([Q1])});
        }
        {
            var Q0;
            Q0=makeQuery(id+"F28.opExtrude","SWEPT_BODY",BODY,{"disambiguationData":[OSD([sQuery(id+"F4.wireOp",EDGE,"E13.0"),sQuery(id+"F4.wireOp",EDGE,"E13.1"),sQuery(id+"F4.wireOp",EDGE,"E13.2"),sQuery(id+"F4.wireOp",EDGE,"E13.3"),sQuery(id+"F4.wireOp",EDGE,"E13.4"),sQuery(id+"F4.wireOp",EDGE,"E13.5")])]});
            transform(context, id + "F50", {"entities" : qUnion([Q0]), "transformType" : TransformType.TRANSLATION_3D, "dx" : 0 * mm, "dy" : 0 * mm, "dz" : 0 * mm, "makeCopy" : true});
        }
    });
